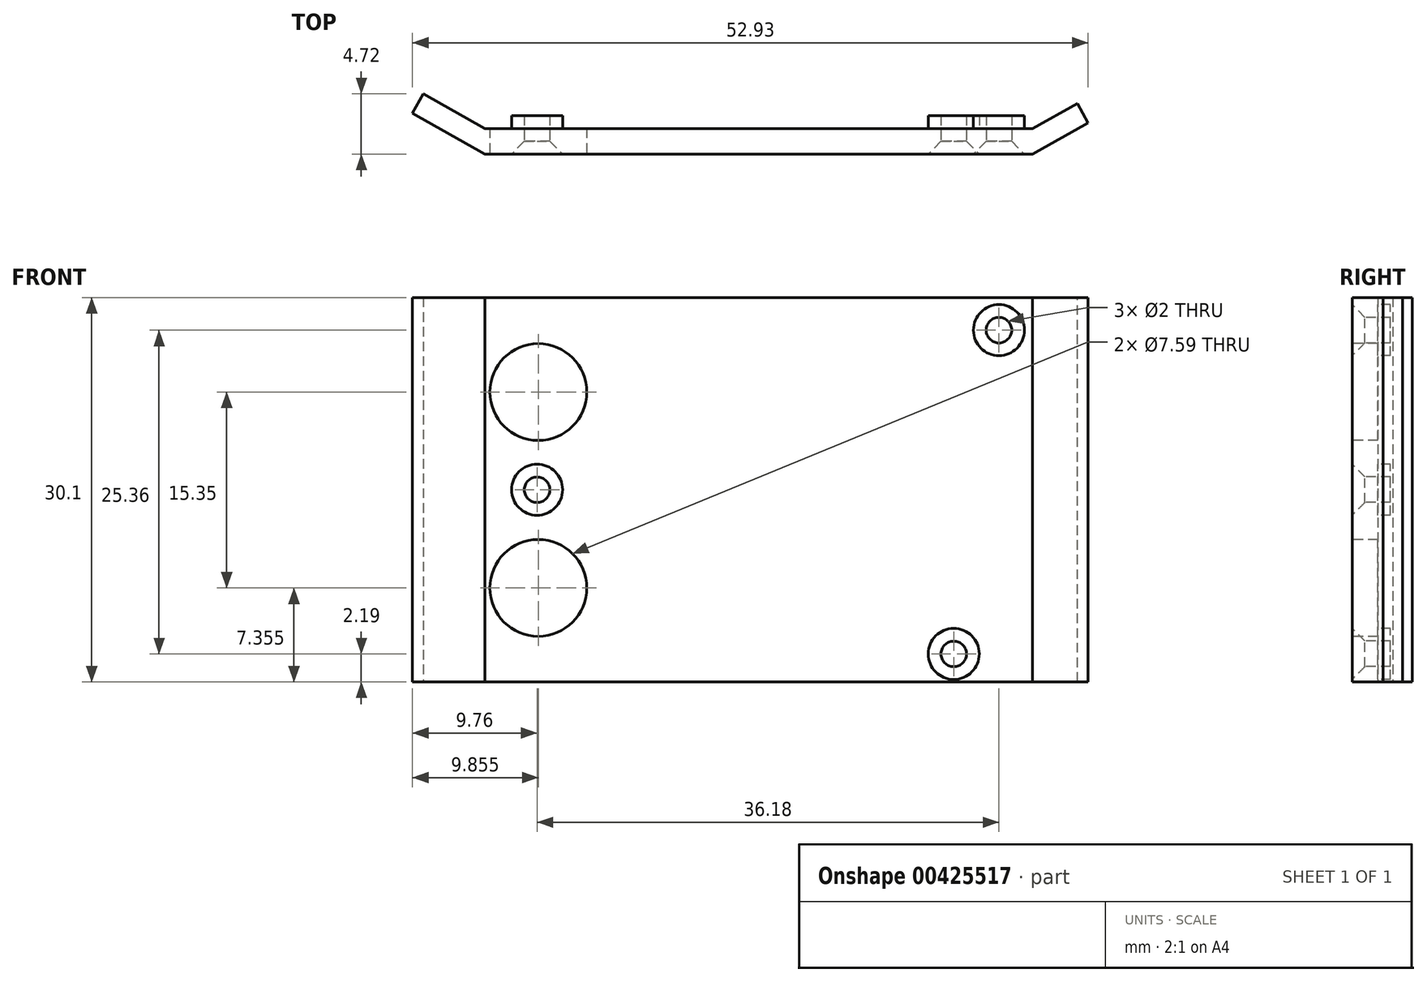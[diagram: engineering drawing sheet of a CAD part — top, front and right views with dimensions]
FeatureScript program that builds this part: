
annotation { "Feature Type Name" : "Feature", "Feature Type Description" : "" }
export const myFeature = defineFeature(function(context is Context, id is Id, definition is map)
    precondition{}
    {
        {
            var Q0;
            Q0=qCreatedBy(makeId("Front.planeOp"),FACE);
            var sketch = newSketch(context, id + "F0", { "sketchPlane" : qUnion([Q0])});
            skLineSegment(sketch, "E0.bottom", {"start": v(21.35, 15.05) * mm, "end": v(-21.35, 15.05) * mm});
            skLineSegment(sketch, "E0.top", {"start": v(21.35, -15.05) * mm, "end": v(-21.35, -15.05) * mm});
            skLineSegment(sketch, "E0.left", {"start": v(21.35, 15.05) * mm, "end": v(21.35, -15.05) * mm});
            skLineSegment(sketch, "E0.right", {"start": v(-21.35, 15.05) * mm, "end": v(-21.35, -15.05) * mm});
            skPoint(sketch, "E0.middle", {"position": v(0, 0) * mm});
            skPoint(sketch, "E1", {"position": v(18.83, 12.5) * mm});
            skPoint(sketch, "E2", {"position": v(15.29, -12.86) * mm});
            skPoint(sketch, "E3", {"position": v(-17.35, 0) * mm});
            skPoint(sketch, "E4", {"position": v(-17.25, 7.66) * mm});
            skPoint(sketch, "E5", {"position": v(-17.25, -7.7) * mm});
            skCircle(sketch, "E6", {"center": v(18.83, 12.5) * mm, "radius": 2 * mm});
            skCircle(sketch, "E7", {"center": v(15.29, -12.86) * mm, "radius": 2 * mm});
            skCircle(sketch, "E8", {"center": v(-17.35, 0) * mm, "radius": 2 * mm});
            skSolve(sketch);
        }
        {
            var Q0;
            Q0=makeQuery(id+"F0.imprint","IMPRINT",FACE,{"disambiguationData":[TD([[makeQuery(id+"F0.imprint","IMPRINT",EDGE,{"derivedFrom":sQuery(id+"F0.wireOp",EDGE,"jPK7hMit-jSFa-N0Mt-JqYe-GtGN3Bu4rccX.bottom")}),1.0]])]});
            var Q1;
            Q1=makeQuery(id+"F0.imprint","IMPRINT",FACE,{"disambiguationData":[TD([[makeQuery(id+"F0.imprint","IMPRINT",EDGE,{"derivedFrom":sQuery(id+"F0.wireOp",EDGE,"E0.bottom")}),1.0]])]});
            var Q2;
            Q2=makeQuery(id+"F0.imprint","IMPRINT",FACE,{"disambiguationData":[TD([[makeQuery(id+"F0.imprint","IMPRINT",EDGE,{"derivedFrom":sQuery(id+"F0.wireOp",EDGE,"e2qhyy3S-mp7l-0j3r-5aax-ppeiUWSRvqxg.bottom")}),1.0]])]});
            var Q3;
            Q3=makeQuery(id+"F0.imprint","IMPRINT",FACE,{"disambiguationData":[TD([[makeQuery(id+"F0.imprint","IMPRINT",EDGE,{"derivedFrom":sQuery(id+"F0.wireOp",EDGE,"aTGAwy4D-jw9e-3WKT-QCMJ-ioXrSI6y0wb3.bottom")}),-1.0]])]});
            var Q4;
            Q4=makeQuery(id+"F0.imprint","IMPRINT",FACE,{"disambiguationData":[TD([[makeQuery(id+"F0.imprint","IMPRINT",EDGE,{"derivedFrom":sQuery(id+"F0.wireOp",EDGE,"E6")}),1.0]])]});
            var Q5;
            Q5=makeQuery(id+"F0.imprint","IMPRINT",FACE,{"disambiguationData":[TD([[makeQuery(id+"F0.imprint","IMPRINT",EDGE,{"derivedFrom":sQuery(id+"F0.wireOp",EDGE,"E8")}),1.0]])]});
            var Q6;
            Q6=makeQuery(id+"F0.imprint","IMPRINT",FACE,{"disambiguationData":[TD([[makeQuery(id+"F0.imprint","IMPRINT",EDGE,{"derivedFrom":sQuery(id+"F0.wireOp",EDGE,"E7")}),1.0]])]});
            extrude(context, id + "F1", {"entities" : qUnion([Q0, Q1, Q2, Q3, Q4, Q5, Q6]), "oppositeDirection" : true, "depth" : 2 * mm});
        }
        {
            var Q0;
            Q0=makeQuery(id+"F0.imprint","IMPRINT",FACE,{"disambiguationData":[TD([[makeQuery(id+"F0.imprint","IMPRINT",EDGE,{"derivedFrom":sQuery(id+"F0.wireOp",EDGE,"E6")}),1.0]])]});
            var Q1;
            Q1=makeQuery(id+"F0.imprint","IMPRINT",FACE,{"disambiguationData":[TD([[makeQuery(id+"F0.imprint","IMPRINT",EDGE,{"derivedFrom":sQuery(id+"F0.wireOp",EDGE,"E7")}),1.0]])]});
            var Q2;
            Q2=makeQuery(id+"F0.imprint","IMPRINT",FACE,{"disambiguationData":[TD([[makeQuery(id+"F0.imprint","IMPRINT",EDGE,{"derivedFrom":sQuery(id+"F0.wireOp",EDGE,"E8")}),1.0]])]});
            extrude(context, id + "F2", {"entities" : qUnion([Q0, Q1, Q2]), "operationType" : NewBodyOperationType.ADD, "oppositeDirection" : true, "depth" : 3 * mm});
        }
        {
            var Q0;
            Q0=makeQuery(id+"F1.opExtrude","SWEPT_FACE",FACE,{"disambiguationData":[OSD([sQuery(id+"F0.wireOp",EDGE,"E0.right")])]});
            extrude(context, id + "F3", {"entities" : qUnion([Q0]), "operationType" : NewBodyOperationType.ADD, "depth" : 0.1 * mm});
        }
        {
            var Q0;
            Q0=makeQuery(id+"F1.opExtrude","SWEPT_FACE",FACE,{"disambiguationData":[OSD([sQuery(id+"F0.wireOp",EDGE,"E0.left")])]});
            extrude(context, id + "F4", {"entities" : qUnion([Q0]), "operationType" : NewBodyOperationType.ADD, "depth" : 0.1 * mm});
        }
        {
            var Q0;
            Q0=makeQuery(id+"F3.opExtrude","CAP_FACE",FACE,{"disambiguationData":[OSD([sQuery(id+"F0.wireOp",EDGE,"E0.right")])],"isStart":false});
            var Q1;
            {var subQ0=sQuery(id+"F0.wireOp",EDGE,"E0.right");Q1=makeQuery(id+"F3.opExtrude","CAP_EDGE",EDGE,{"disambiguationData":[OSD([subQ0]),TDD([makeQuery(id+"F1.opExtrude","CAP_EDGE",EDGE,{"disambiguationData":[OSD([subQ0])],"isStart":true})])],"isStart":false});}
            cPlane(context, id + "F5", {"entities" : qUnion([Q0, Q1]), "cplaneType" : CPlaneType.LINE_ANGLE, "offset" : 25 * mm, "angle" : 29.5 * degree, "width" : 150 * mm, "height" : 150 * mm});
        }
        {
            var Q0;
            Q0=qCreatedBy(id+"F5.planeOp",FACE);
            var sketch = newSketch(context, id + "F6", { "sketchPlane" : qUnion([Q0])});
            skLineSegment(sketch, "E9.bottom", {"start": v(-8.82, 15.05) * mm, "end": v(-10.56, 15.05) * mm});
            skLineSegment(sketch, "E9.top", {"start": v(-8.82, -15.05) * mm, "end": v(-10.56, -15.05) * mm});
            skLineSegment(sketch, "E9.left", {"start": v(-8.82, 15.05) * mm, "end": v(-8.82, -15.05) * mm});
            skLineSegment(sketch, "E9.right", {"start": v(-10.56, 15.05) * mm, "end": v(-10.56, -15.05) * mm});
            skSolve(sketch);
        }
        {
            var Q0;
            Q0=qSketchRegion(id+"F6",true);
            extrude(context, id + "F7", {"entities" : qUnion([Q0]), "operationType" : NewBodyOperationType.ADD, "oppositeDirection" : true, "depth" : 6.5 * mm});
        }
        {
            var Q0;
            Q0=makeQuery(id+"F4.opExtrude","CAP_FACE",FACE,{"disambiguationData":[OSD([sQuery(id+"F0.wireOp",EDGE,"E0.left")])],"isStart":false});
            var Q1;
            {var subQ0=sQuery(id+"F0.wireOp",EDGE,"E0.left");Q1=makeQuery(id+"F4.opExtrude","CAP_EDGE",EDGE,{"disambiguationData":[OSD([subQ0]),TDD([makeQuery(id+"F1.opExtrude","CAP_EDGE",EDGE,{"disambiguationData":[OSD([subQ0])],"isStart":true})])],"isStart":false});}
            cPlane(context, id + "F8", {"entities" : qUnion([Q0, Q1]), "cplaneType" : CPlaneType.LINE_ANGLE, "offset" : 25 * mm, "angle" : 29 * degree, "oppositeDirection" : true, "width" : 150 * mm, "height" : 150 * mm});
        }
        {
            var Q0;
            Q0=qCreatedBy(id+"F8.planeOp",FACE);
            var sketch = newSketch(context, id + "F9", { "sketchPlane" : qUnion([Q0])});
            skLineSegment(sketch, "E10.bottom", {"start": v(10.4, -15.05) * mm, "end": v(8.65, -15.05) * mm});
            skLineSegment(sketch, "E10.top", {"start": v(10.4, 15.05) * mm, "end": v(8.65, 15.05) * mm});
            skLineSegment(sketch, "E10.left", {"start": v(10.4, -15.05) * mm, "end": v(10.4, 15.05) * mm});
            skLineSegment(sketch, "E10.right", {"start": v(8.65, -15.05) * mm, "end": v(8.65, 15.05) * mm});
            skSolve(sketch);
        }
        {
            var Q0;
            Q0=qSketchRegion(id+"F9",true);
            extrude(context, id + "F10", {"entities" : qUnion([Q0]), "operationType" : NewBodyOperationType.ADD, "oppositeDirection" : true, "depth" : 5 * mm});
        }
        {
            var Q0;
            Q0=sQuery(id+"F0.wireOp",VERTEX,"E3");
            var Q1;
            Q1=sQuery(id+"F0.wireOp",VERTEX,"E1");
            var Q2;
            Q2=sQuery(id+"F0.wireOp",VERTEX,"E2");
            var Q3;
            Q3=makeQuery(id+"F1.opExtrude","SWEPT_BODY",BODY,{"disambiguationData":[OSD([sQuery(id+"F0.wireOp",EDGE,"E0.bottom"),sQuery(id+"F0.wireOp",EDGE,"E0.top"),sQuery(id+"F0.wireOp",EDGE,"E0.left"),sQuery(id+"F0.wireOp",EDGE,"E0.right")])]});
            hole(context, id + "F11", {"style" : HoleStyle.C_SINK, "endStyle" : HoleEndStyle.THROUGH, "holeDiameter" : 2 * mm, "cSinkDiameter" : 4 * mm, "cSinkAngle" : 90 * degree, "isTappedThrough" : true, "tappedDepth" : 12 * mm, "tapClearance" : 3, "locations" : qUnion([Q0, Q1, Q2]), "scope" : qUnion([Q3])});
        }
        {
            var Q0;
            Q0=sQuery(id+"F0.wireOp",VERTEX,"E4");
            var Q1;
            Q1=sQuery(id+"F0.wireOp",VERTEX,"E5");
            var Q2;
            Q2=makeQuery(id+"F1.opExtrude","SWEPT_BODY",BODY,{"disambiguationData":[OSD([sQuery(id+"F0.wireOp",EDGE,"E0.bottom"),sQuery(id+"F0.wireOp",EDGE,"E0.top"),sQuery(id+"F0.wireOp",EDGE,"E0.left"),sQuery(id+"F0.wireOp",EDGE,"E0.right")])]});
            hole(context, id + "F12", {"style" : HoleStyle.SIMPLE, "endStyle" : HoleEndStyle.THROUGH, "holeDiameter" : 7.6 * mm, "isTappedThrough" : true, "tappedDepth" : 12 * mm, "tapClearance" : 3, "locations" : qUnion([Q0, Q1]), "scope" : qUnion([Q2])});
        }
    });
